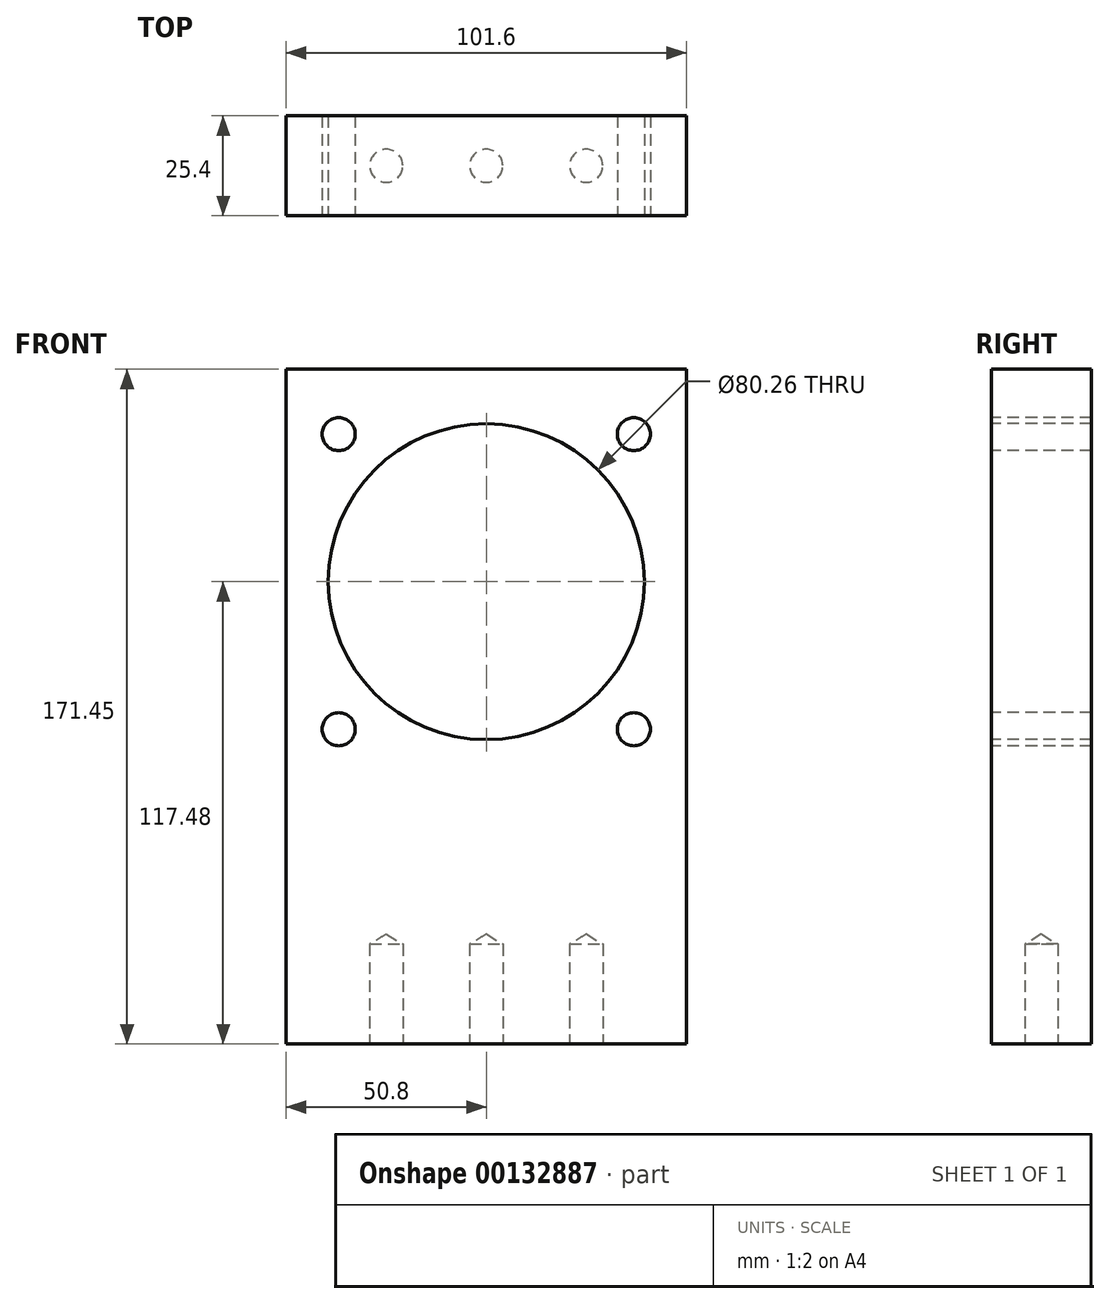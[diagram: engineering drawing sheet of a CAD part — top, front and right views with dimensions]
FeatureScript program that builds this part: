
annotation { "Feature Type Name" : "Feature", "Feature Type Description" : "" }
export const myFeature = defineFeature(function(context is Context, id is Id, definition is map)
    precondition{}
    {
        {
            var Q0;
            Q0=qCreatedBy(makeId("Front.planeOp"),FACE);
            var sketch = newSketch(context, id + "F0", { "sketchPlane" : qUnion([Q0])});
            skLineSegment(sketch, "E0.bottom", {"start": v(-50.8, 85.73) * mm, "end": v(50.8, 85.73) * mm});
            skLineSegment(sketch, "E0.top", {"start": v(-50.8, -85.73) * mm, "end": v(50.8, -85.73) * mm});
            skLineSegment(sketch, "E0.left", {"start": v(-50.8, 85.73) * mm, "end": v(-50.8, -85.73) * mm});
            skLineSegment(sketch, "E0.right", {"start": v(50.8, 85.73) * mm, "end": v(50.8, -85.73) * mm});
            skPoint(sketch, "E0.middle", {"position": v(0, 0) * mm});
            skSolve(sketch);
        }
        {
            var Q0;
            Q0=makeQuery(id+"F0.imprint","IMPRINT",FACE,{"disambiguationData":[TD([[makeQuery(id+"F0.imprint","IMPRINT",EDGE,{"derivedFrom":sQuery(id+"F0.wireOp",EDGE,"E0.bottom")}),-1.0]])]});
            extrude(context, id + "F1", {"entities" : qUnion([Q0]), "depth" : 25.4 * mm});
        }
        {
            var Q0;
            Q0=makeQuery(id+"F1.opExtrude","SWEPT_FACE",FACE,{"disambiguationData":[OSD([sQuery(id+"F0.wireOp",EDGE,"E0.top")])]});
            var sketch = newSketch(context, id + "F2", { "sketchPlane" : qUnion([Q0])});
            skPoint(sketch, "E1", {"position": v(-25.4, 12.7) * mm});
            skPoint(sketch, "E2", {"position": v(25.4, 12.7) * mm});
            skPoint(sketch, "E3", {"position": v(0, 12.7) * mm});
            skSolve(sketch);
        }
        {
            var Q0;
            Q0=sQuery(id+"F2.wireOp",VERTEX,"E1");
            var Q1;
            Q1=sQuery(id+"F2.wireOp",VERTEX,"E2");
            var Q2;
            Q2=sQuery(id+"F2.wireOp",VERTEX,"E3");
            var Q3;
            Q3=makeQuery(id+"F1.opExtrude","SWEPT_BODY",BODY,{"disambiguationData":[OSD([sQuery(id+"F0.wireOp",EDGE,"E0.bottom"),sQuery(id+"F0.wireOp",EDGE,"E0.top"),sQuery(id+"F0.wireOp",EDGE,"E0.left"),sQuery(id+"F0.wireOp",EDGE,"E0.right")])]});
            hole(context, id + "F3", {"style" : HoleStyle.SIMPLE, "endStyle" : HoleEndStyle.BLIND, "standardTappedOrClearance" : lookupTablePath({ "standard" : "ANSI", "engagement" : "75%", "pitch" : "24 tpi", "size" : "3/8", "type" : "Tapped" }), "standardBlindInLast" : lookupTablePath({ "standard" : "ANSI", "engagement" : "75%", "pitch" : "24 tpi", "size" : "3/8", "type" : "Tapped" }), "holeDiameter" : 8.43 * mm, "holeDepth" : 25.4 * mm, "locations" : qUnion([Q0, Q1, Q2]), "scope" : qUnion([Q3]), "majorDiameter" : 9.53 * mm});
        }
        {
            var Q0;
            Q0=makeQuery(id+"F1.opExtrude","CAP_FACE",FACE,{"disambiguationData":[OSD([sQuery(id+"F0.wireOp",EDGE,"E0.bottom"),sQuery(id+"F0.wireOp",EDGE,"E0.top"),sQuery(id+"F0.wireOp",EDGE,"E0.left"),sQuery(id+"F0.wireOp",EDGE,"E0.right")])],"isStart":false});
            var sketch = newSketch(context, id + "F4", { "sketchPlane" : qUnion([Q0])});
            skCircle(sketch, "E4", {"center": v(0, 31.75) * mm, "radius": 40.13 * mm});
            skSolve(sketch);
        }
        {
            var Q0;
            Q0=makeQuery(id+"F4.imprint","IMPRINT",FACE,{"disambiguationData":[TD([[makeQuery(id+"F4.imprint","IMPRINT",EDGE,{"derivedFrom":sQuery(id+"F4.wireOp",EDGE,"E4")}),1.0]])]});
            extrude(context, id + "F5", {"entities" : qUnion([Q0]), "operationType" : NewBodyOperationType.REMOVE, "endBound" : BoundingType.THROUGH_ALL, "oppositeDirection" : true, "depth" : 25.4 * mm});
        }
        {
            var Q0;
            Q0=makeQuery(id+"F1.opExtrude","CAP_FACE",FACE,{"disambiguationData":[OSD([sQuery(id+"F0.wireOp",EDGE,"E0.bottom"),sQuery(id+"F0.wireOp",EDGE,"E0.top"),sQuery(id+"F0.wireOp",EDGE,"E0.left"),sQuery(id+"F0.wireOp",EDGE,"E0.right")])],"isStart":false});
            var sketch = newSketch(context, id + "F6", { "sketchPlane" : qUnion([Q0])});
            skPoint(sketch, "E5", {"position": v(-37.5, 69.24) * mm});
            skPoint(sketch, "E6", {"position": v(37.5, 69.24) * mm});
            skPoint(sketch, "E7", {"position": v(37.5, -5.74) * mm});
            skPoint(sketch, "E8", {"position": v(-37.5, -5.74) * mm});
            skCircle(sketch, "E9.0", {"center": v(0, 31.75) * mm, "radius": 40.13 * mm});
            skLineSegment(sketch, "E10", {"start": v(0, 31.75) * mm, "end": v(0, 69.24) * mm, "construction": true});
            skLineSegment(sketch, "E11", {"start": v(0, 31.75) * mm, "end": v(0, -5.74) * mm, "construction": true});
            skLineSegment(sketch, "E12", {"start": v(0, 31.75) * mm, "end": v(37.5, 31.75) * mm, "construction": true});
            skLineSegment(sketch, "E13", {"start": v(0, 31.75) * mm, "end": v(-37.5, 31.75) * mm, "construction": true});
            skSolve(sketch);
        }
        {
            var Q0;
            Q0=sQuery(id+"F6.wireOp",VERTEX,"E5");
            var Q1;
            Q1=sQuery(id+"F6.wireOp",VERTEX,"E6");
            var Q2;
            Q2=sQuery(id+"F6.wireOp",VERTEX,"E7");
            var Q3;
            Q3=sQuery(id+"F6.wireOp",VERTEX,"E8");
            var Q4;
            Q4=makeQuery(id+"F1.opExtrude","SWEPT_BODY",BODY,{"disambiguationData":[OSD([sQuery(id+"F0.wireOp",EDGE,"E0.bottom"),sQuery(id+"F0.wireOp",EDGE,"E0.top"),sQuery(id+"F0.wireOp",EDGE,"E0.left"),sQuery(id+"F0.wireOp",EDGE,"E0.right")])]});
            hole(context, id + "F7", {"style" : HoleStyle.SIMPLE, "endStyle" : HoleEndStyle.THROUGH, "standardTappedOrClearance" : lookupTablePath({ "standard" : "ISO", "fit" : "Close", "size" : "M8", "type" : "Clearance" }), "standardBlindInLast" : lookupTablePath({ "fit" : "Close", "standard" : "ISO", "size" : "M8", "type" : "Clearance" }), "holeDiameter" : 8.4 * mm, "locations" : qUnion([Q0, Q1, Q2, Q3]), "scope" : qUnion([Q4]), "isTappedThrough" : true});
        }
    });
